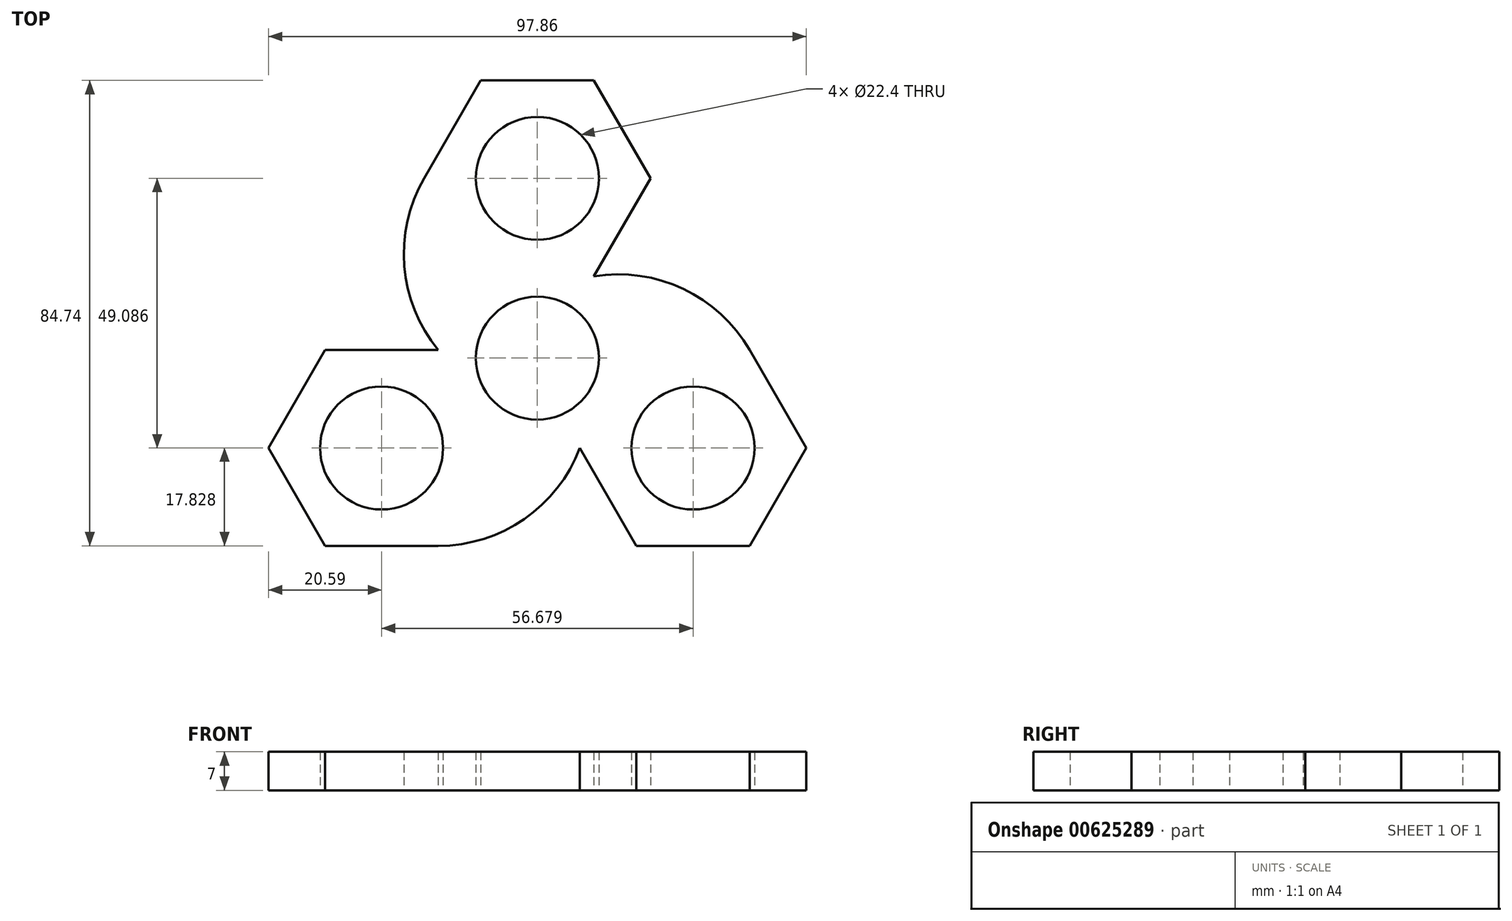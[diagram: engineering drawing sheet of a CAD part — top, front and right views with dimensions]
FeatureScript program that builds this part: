
annotation { "Feature Type Name" : "Feature", "Feature Type Description" : "" }
export const myFeature = defineFeature(function(context is Context, id is Id, definition is map)
    precondition{}
    {
        {
            var Q0;
            Q0=qCreatedBy(makeId("Top.planeOp"),FACE);
            var sketch = newSketch(context, id + "F0", { "sketchPlane" : qUnion([Q0])});
            skCircle(sketch, "E0", {"center": v(0, 0) * mm, "radius": 11.2 * mm});
            skArc(sketch, "E1", {"start": v(11.38, -10.08) * mm, "mid": v(13.16, -7.6) * mm, "end": v(14.42, -4.81) * mm});
            skCircle(sketch, "E2", {"center": v(0, 32.72) * mm, "radius": 11.2 * mm});
            skArc(sketch, "E3.cCircle", {"start": v(7.15, 13.41) * mm, "mid": v(0, 53.31) * mm, "end": v(-7.15, 13.41) * mm, "construction": true});
            skLineSegment(sketch, "E3.0", {"start": v(-20.59, 32.72) * mm, "end": v(-10.3, 50.55) * mm});
            skLineSegment(sketch, "E3.1", {"start": v(-10.3, 50.55) * mm, "end": v(10.3, 50.55) * mm});
            skLineSegment(sketch, "E3.2", {"start": v(10.3, 50.55) * mm, "end": v(20.59, 32.72) * mm});
            skLineSegment(sketch, "E3.3", {"start": v(20.59, 32.72) * mm, "end": v(10.3, 14.9) * mm});
            skLineSegment(sketch, "E3.4", {"start": v(10.3, 14.9) * mm, "end": v(-10.3, 14.9) * mm});
            skLineSegment(sketch, "E3.5", {"start": v(-10.3, 14.9) * mm, "end": v(-20.59, 32.72) * mm});
            skLineSegment(sketch, "E4.1.0", {"start": v(-18.05, -34.2) * mm, "end": v(-38.63, -34.2) * mm});
            skLineSegment(sketch, "E4.1.1", {"start": v(-38.63, -34.2) * mm, "end": v(-48.93, -16.36) * mm});
            skLineSegment(sketch, "E4.1.2", {"start": v(-48.93, -16.36) * mm, "end": v(-38.63, 1.47) * mm});
            skLineSegment(sketch, "E4.1.3", {"start": v(-38.63, 1.47) * mm, "end": v(-18.05, 1.47) * mm});
            skLineSegment(sketch, "E4.1.4", {"start": v(-18.05, 1.47) * mm, "end": v(-7.75, -16.36) * mm});
            skLineSegment(sketch, "E4.1.5", {"start": v(-7.75, -16.36) * mm, "end": v(-18.05, -34.2) * mm});
            skLineSegment(sketch, "E4.2.0", {"start": v(38.63, 1.47) * mm, "end": v(48.93, -16.36) * mm});
            skLineSegment(sketch, "E4.2.1", {"start": v(48.93, -16.36) * mm, "end": v(38.63, -34.2) * mm});
            skLineSegment(sketch, "E4.2.2", {"start": v(38.63, -34.2) * mm, "end": v(18.05, -34.2) * mm});
            skLineSegment(sketch, "E4.2.3", {"start": v(18.05, -34.2) * mm, "end": v(7.75, -16.36) * mm});
            skLineSegment(sketch, "E4.2.4", {"start": v(7.75, -16.36) * mm, "end": v(11.38, -10.08) * mm});
            skLineSegment(sketch, "E4.2.5", {"start": v(18.05, 1.47) * mm, "end": v(38.63, 1.47) * mm});
            skArc(sketch, "E5", {"start": v(-20.59, 32.72) * mm, "mid": v(-24.2, 16.7) * mm, "end": v(-18.05, 1.47) * mm});
            skArc(sketch, "E6.1.0", {"start": v(-18.05, -34.2) * mm, "mid": v(-2.37, -29.3) * mm, "end": v(7.75, -16.36) * mm});
            skArc(sketch, "E6.2.0", {"start": v(38.63, 1.47) * mm, "mid": v(26.56, 12.6) * mm, "end": v(10.3, 14.9) * mm});
            skCircle(sketch, "E7.1.0", {"center": v(-28.34, -16.36) * mm, "radius": 11.2 * mm});
            skCircle(sketch, "E7.2.0", {"center": v(28.34, -16.36) * mm, "radius": 11.2 * mm});
            skArc(sketch, "E8.trimOffspring", {"start": v(7.15, 13.41) * mm, "mid": v(5.15, 14.3) * mm, "end": v(3.04, 14.9) * mm});
            skLineSegment(sketch, "E9.trimOffspring", {"start": v(14.42, -4.81) * mm, "end": v(18.05, 1.47) * mm});
            skArc(sketch, "E10.trimOffspring", {"start": v(-3.04, 14.9) * mm, "mid": v(-5.15, 14.3) * mm, "end": v(-7.15, 13.41) * mm});
            skSolve(sketch);
        }
        {
            var Q0;
            Q0=makeQuery(id+"F0.imprint","IMPRINT",FACE,{"disambiguationData":[TD([[makeQuery(id+"F0.imprint","IMPRINT",EDGE,{"derivedFrom":sQuery(id+"F0.wireOp",EDGE,"E0")}),-1.0]])]});
            var Q1;
            Q1=makeQuery(id+"F0.imprint","IMPRINT",FACE,{"disambiguationData":[TD([[makeQuery(id+"F0.imprint","IMPRINT",EDGE,{"derivedFrom":sQuery(id+"F0.wireOp",EDGE,"E4.1.0")}),-1.0]])]});
            var Q2;
            {var subQ0=sQuery(id+"F0.wireOp",EDGE,"E1");Q2=makeQuery(id+"F0.imprint","IMPRINT",FACE,{"disambiguationData":[TD([[makeQuery(id+"F0.imprint","IMPRINT",EDGE,{"derivedFrom":subQ0}),-1.0]])]});}
            var Q3;
            Q3=makeQuery(id+"F0.imprint","IMPRINT",FACE,{"disambiguationData":[TD([[makeQuery(id+"F0.imprint","IMPRINT",EDGE,{"derivedFrom":sQuery(id+"F0.wireOp",EDGE,"E2")}),-1.0]])]});
            extrude(context, id + "F1", {"entities" : qUnion([Q0, Q1, Q2, Q3]), "depth" : 7 * mm, "offsetDistance" : 25 * mm});
        }
    });
